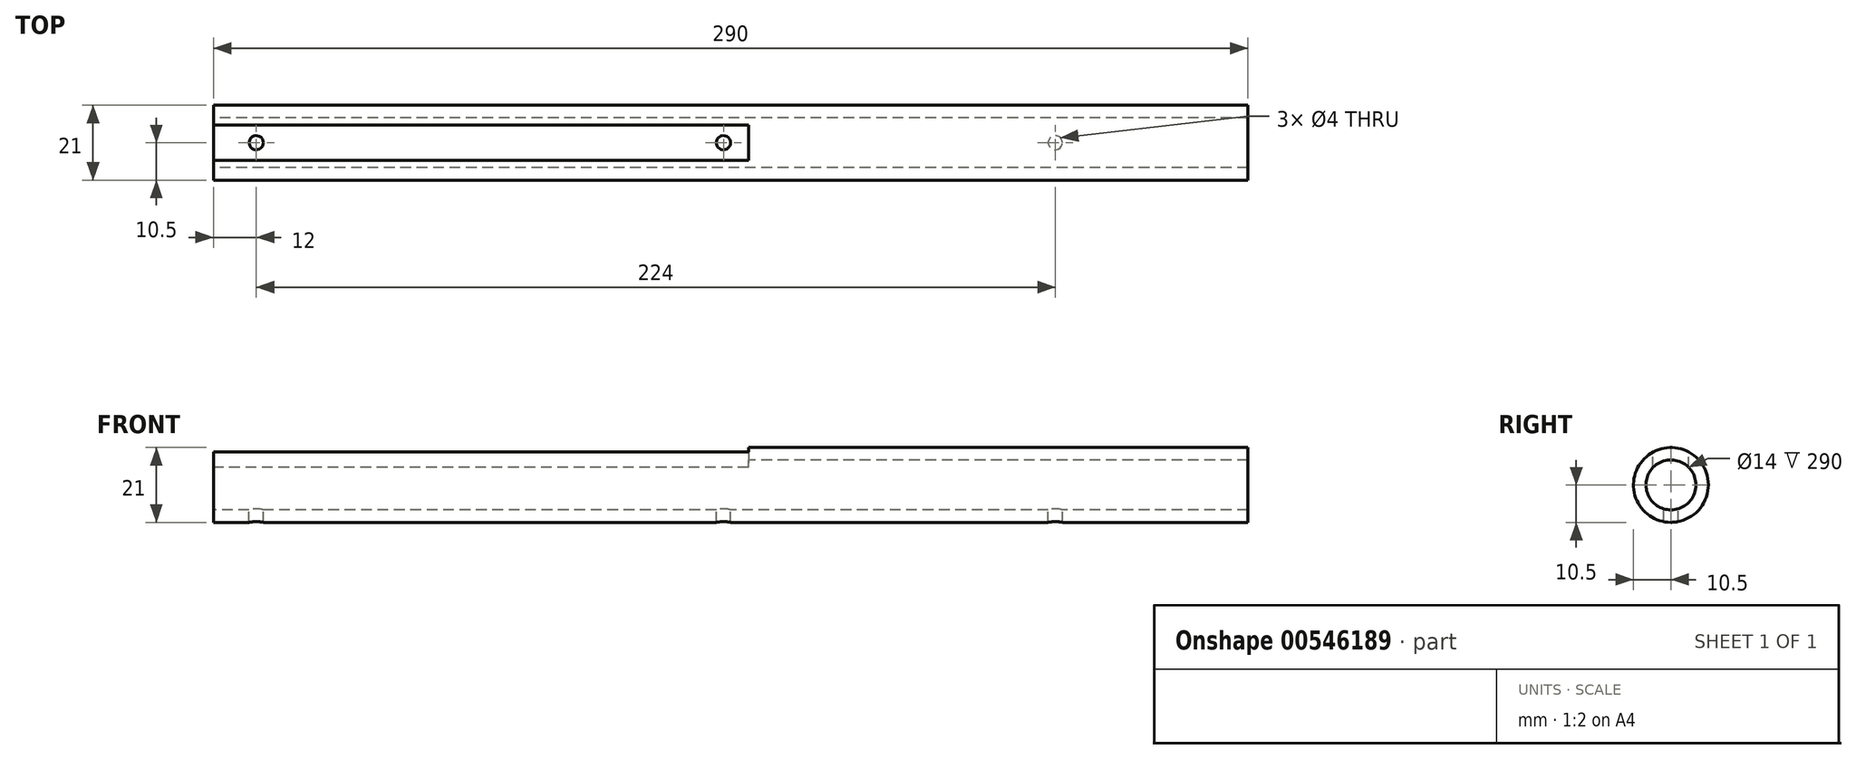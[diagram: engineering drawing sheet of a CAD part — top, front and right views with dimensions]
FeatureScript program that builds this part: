
annotation { "Feature Type Name" : "Feature", "Feature Type Description" : "" }
export const myFeature = defineFeature(function(context is Context, id is Id, definition is map)
    precondition{}
    {
        {
            var Q0;
            Q0=qCreatedBy(makeId("Right.planeOp"),FACE);
            var sketch = newSketch(context, id + "F0", { "sketchPlane" : qUnion([Q0])});
            skCircle(sketch, "E0", {"center": v(0, 0) * mm, "radius": 10.5 * mm});
            skSolve(sketch);
        }
        {
            var Q0;
            Q0 = qSketchRegion(id + "F0", true);
            extrude(context, id + "F1", {"entities" : qUnion([Q0]), "depth" : 290 * mm, "offsetDistance" : 25 * mm});
        }
        {
            var Q0;
            Q0=makeQuery(id+"F1.opExtrude","CAP_FACE",FACE,{"disambiguationData":[OSD([sQuery(id+"F0.wireOp",EDGE,"E0")])],"isStart":true});
            var sketch = newSketch(context, id + "F2", { "sketchPlane" : qUnion([Q0])});
            skCircle(sketch, "E1", {"center": v(0, 0) * mm, "radius": 7 * mm});
            skSolve(sketch);
        }
        {
            var Q0;
            Q0 = qSketchRegion(id + "F2", true);
            extrude(context, id + "F3", {"entities" : qUnion([Q0]), "operationType" : NewBodyOperationType.REMOVE, "oppositeDirection" : true, "depth" : 300 * mm, "offsetDistance" : 25 * mm});
        }
        {
            var Q0;
            Q0=qCreatedBy(makeId("Top.planeOp"),FACE);
            var sketch = newSketch(context, id + "F4", { "sketchPlane" : qUnion([Q0])});
            skLineSegment(sketch, "E2", {"start": v(0, 0) * mm, "end": v(45, 0) * mm});
            skLineSegment(sketch, "E3.bottom", {"start": v(32.5, 3) * mm, "end": v(57.5, 3) * mm});
            skLineSegment(sketch, "E3.top", {"start": v(32.5, -3) * mm, "end": v(57.5, -3) * mm});
            skLineSegment(sketch, "E3.left", {"start": v(32.5, 3) * mm, "end": v(32.5, -3) * mm});
            skLineSegment(sketch, "E3.right", {"start": v(57.5, 3) * mm, "end": v(57.5, -3) * mm});
            skPoint(sketch, "E3.middle", {"position": v(45, 0) * mm});
            skSolve(sketch);
        }
        {
            var Q0;
            Q0=qCreatedBy(makeId("Top.planeOp"),FACE);
            var sketch = newSketch(context, id + "F5", { "sketchPlane" : qUnion([Q0])});
            skLineSegment(sketch, "E4", {"start": v(0, 0) * mm, "end": v(0, 0) * mm});
            skLineSegment(sketch, "E5.bottom", {"start": v(-150, 5) * mm, "end": v(150, 5) * mm});
            skLineSegment(sketch, "E5.top", {"start": v(-150, -5) * mm, "end": v(150, -5) * mm});
            skLineSegment(sketch, "E5.left", {"start": v(-150, 5) * mm, "end": v(-150, -5) * mm});
            skLineSegment(sketch, "E5.right", {"start": v(150, 5) * mm, "end": v(150, -5) * mm});
            skPoint(sketch, "E5.middle", {"position": v(0, 0) * mm});
            skSolve(sketch);
        }
        {
            var Q0;
            Q0 = qSketchRegion(id + "F5", true);
            extrude(context, id + "F6", {"entities" : qUnion([Q0]), "operationType" : NewBodyOperationType.REMOVE, "depth" : 25 * mm, "offsetDistance" : 25 * mm});
        }
        {
            var Q0;
            Q0=qCreatedBy(makeId("Top.planeOp"),FACE);
            var sketch = newSketch(context, id + "F7", { "sketchPlane" : qUnion([Q0])});
            skLineSegment(sketch, "E6", {"start": v(0, 0) * mm, "end": v(12, 0) * mm});
            skCircle(sketch, "E7", {"center": v(12, 0) * mm, "radius": 2 * mm});
            skLineSegment(sketch, "E8", {"start": v(12, 0) * mm, "end": v(143, 0) * mm});
            skCircle(sketch, "E9", {"center": v(143, 0) * mm, "radius": 2 * mm});
            skLineSegment(sketch, "E10", {"start": v(143, 0) * mm, "end": v(236, 0) * mm});
            skCircle(sketch, "E11", {"center": v(236, 0) * mm, "radius": 2 * mm});
            skSolve(sketch);
        }
        {
            var Q0;
            Q0 = qSketchRegion(id + "F7", true);
            extrude(context, id + "F8", {"entities" : qUnion([Q0]), "operationType" : NewBodyOperationType.REMOVE, "oppositeDirection" : true, "depth" : 25 * mm, "offsetDistance" : 25 * mm});
        }
    });
